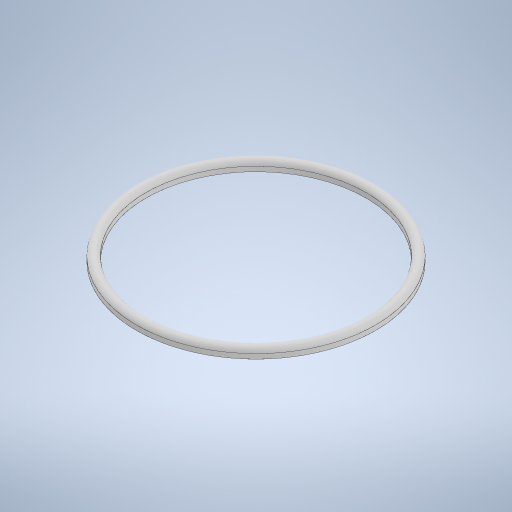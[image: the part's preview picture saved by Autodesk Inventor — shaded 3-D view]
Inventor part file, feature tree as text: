
AUTODESK INVENTOR PART (.ipt)
format: ipt  version: 2023 (Build 270158030, 158C)  size: 260,608 bytes
history: native  units: in
note: dims shown in document units (in); Inventor stores cm internally (conversion verified against a paired STEP export)
features: revolve x1, sketch x1
ambient origin geometry x8: Origin, YZ Plane, XZ Plane, XY Plane, X Axis, Y Axis, Z Axis, Center Point
bodies: Solid1 (feature_tree)
feature tree (2):
  revolve  "Revolution1"  [1 undecoded]
  sketch  "Sketch1"  dims[d0=0.125in d1=3.0in d3=0.125in d4=90.0deg]
note: 1 required parameter value undecoded (feature->parameter linkage not recoverable at this tier; creation-order binding heuristic only, values carry confidence <= 0.55)
